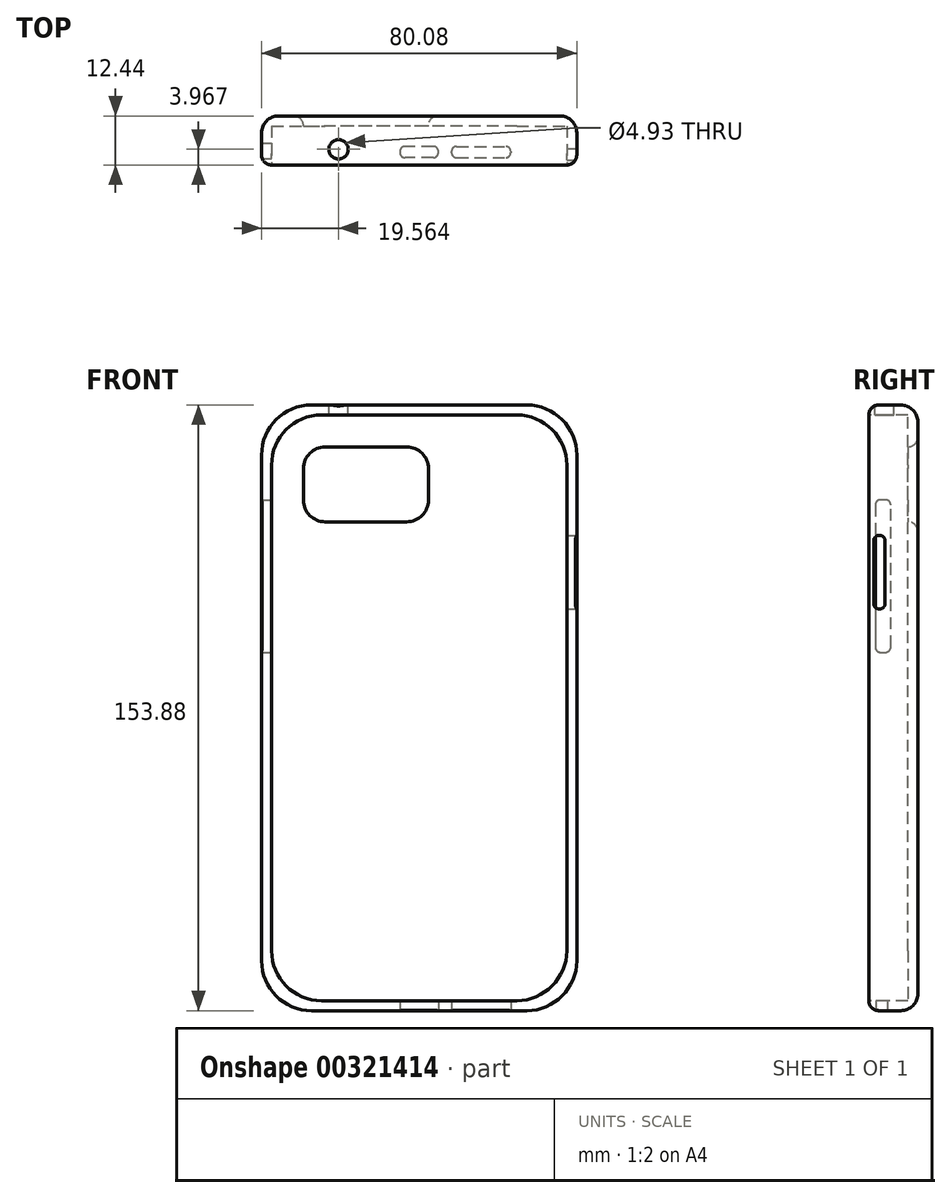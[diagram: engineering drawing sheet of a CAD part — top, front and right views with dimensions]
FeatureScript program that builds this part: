
annotation { "Feature Type Name" : "Feature", "Feature Type Description" : "" }
export const myFeature = defineFeature(function(context is Context, id is Id, definition is map)
    precondition{}
    {
        {
            var Q0;
            Q0=qCreatedBy(makeId("Front.planeOp"),FACE);
            var sketch = newSketch(context, id + "F0", { "sketchPlane" : qUnion([Q0])});
            skLineSegment(sketch, "E0", {"start": v(-36.95, 74.5) * mm, "end": v(38.05, 74.5) * mm});
            skLineSegment(sketch, "E1", {"start": v(38.05, 74.5) * mm, "end": v(38.05, -74.3) * mm});
            skLineSegment(sketch, "E2", {"start": v(38.05, -74.3) * mm, "end": v(-36.95, -74.3) * mm});
            skLineSegment(sketch, "E3", {"start": v(-36.95, -74.3) * mm, "end": v(-36.95, 74.5) * mm});
            skSolve(sketch);
        }
        {
            var Q0;
            Q0=makeQuery(id+"F0.imprint","IMPRINT",FACE,{"disambiguationData":[TD([[makeQuery(id+"F0.imprint","IMPRINT",EDGE,{"derivedFrom":sQuery(id+"F0.wireOp",EDGE,"E0")}),-1.0]])]});
            extrude(context, id + "F1", {"entities" : qUnion([Q0]), "oppositeDirection" : true, "depth" : 9.9 * mm});
        }
        {
            var Q0;
            Q0=makeQuery(id+"F1.opExtrude","SWEPT_FACE",FACE,{"disambiguationData":[OSD([sQuery(id+"F0.wireOp",EDGE,"E3")])]});
            var sketch = newSketch(context, id + "F2", { "sketchPlane" : qUnion([Q0])});
            skLineSegment(sketch, "E4", {"start": v(-5.56, 52.95) * mm, "end": v(-1.65, 52.95) * mm});
            skLineSegment(sketch, "E5", {"start": v(-1.65, 52.95) * mm, "end": v(-1.65, 14.2) * mm});
            skLineSegment(sketch, "E6", {"start": v(-1.65, 14.2) * mm, "end": v(-5.56, 14.2) * mm});
            skLineSegment(sketch, "E7", {"start": v(-5.56, 14.2) * mm, "end": v(-5.56, 52.95) * mm});
            skSolve(sketch);
        }
        {
            var Q0;
            Q0=makeQuery(id+"F1.opExtrude","CAP_FACE",FACE,{"disambiguationData":[OSD([sQuery(id+"F0.wireOp",EDGE,"E0"),sQuery(id+"F0.wireOp",EDGE,"E1"),sQuery(id+"F0.wireOp",EDGE,"E2"),sQuery(id+"F0.wireOp",EDGE,"E3")])],"isStart":true});
            shell(context, id + "F3", {"entities" : qUnion([Q0]), "thickness" : 2.54 * mm, "oppositeDirection" : true});
        }
        {
            var Q0;
            Q0=makeQuery(id+"F2.imprint","IMPRINT",FACE,{"disambiguationData":[TD([[makeQuery(id+"F2.imprint","IMPRINT",EDGE,{"derivedFrom":sQuery(id+"F2.wireOp",EDGE,"E4")}),-1.0]])]});
            extrude(context, id + "F4", {"entities" : qUnion([Q0]), "operationType" : NewBodyOperationType.REMOVE, "oppositeDirection" : true, "depth" : 25.4 * mm});
        }
        {
            var Q0;
            Q0=makeQuery(id+"F1.opExtrude","CAP_EDGE",EDGE,{"disambiguationData":[OSD([sQuery(id+"F0.wireOp",EDGE,"E1")])],"isStart":false});
            var Q1;
            Q1=makeQuery(id+"F1.opExtrude","CAP_EDGE",EDGE,{"disambiguationData":[OSD([sQuery(id+"F0.wireOp",EDGE,"E0")])],"isStart":false});
            var Q2;
            Q2=makeQuery(id+"F1.opExtrude","CAP_EDGE",EDGE,{"disambiguationData":[OSD([sQuery(id+"F0.wireOp",EDGE,"E3")])],"isStart":false});
            var Q3;
            Q3=makeQuery(id+"F1.opExtrude","CAP_EDGE",EDGE,{"disambiguationData":[OSD([sQuery(id+"F0.wireOp",EDGE,"E2")])],"isStart":false});
            fillet(context, id + "F5", {"entities" : qUnion([Q0, Q1, Q2, Q3]), "radius" : 4.3 * mm, "tangentPropagation" : true, "allowEdgeOverflow" : false});
        }
        {
            var Q0;
            Q0=makeQuery(id+"F1.opExtrude","SWEPT_FACE",FACE,{"disambiguationData":[OSD([sQuery(id+"F0.wireOp",EDGE,"E1")])]});
            var sketch = newSketch(context, id + "F6", { "sketchPlane" : qUnion([Q0])});
            skLineSegment(sketch, "E8", {"start": v(1.26, 43.9) * mm, "end": v(4.1, 43.9) * mm});
            skLineSegment(sketch, "E9", {"start": v(4.1, 43.9) * mm, "end": v(4.1, 25.22) * mm});
            skLineSegment(sketch, "E10", {"start": v(4.1, 25.22) * mm, "end": v(1.26, 25.22) * mm});
            skLineSegment(sketch, "E11", {"start": v(1.26, 25.22) * mm, "end": v(1.26, 43.9) * mm});
            skSolve(sketch);
        }
        {
            var Q0;
            Q0=makeQuery(id+"F1.opExtrude","SWEPT_FACE",FACE,{"disambiguationData":[OSD([sQuery(id+"F0.wireOp",EDGE,"E2")])]});
            var sketch = newSketch(context, id + "F7", { "sketchPlane" : qUnion([Q0])});
            skLineSegment(sketch, "E12", {"start": v(-4.33, -1.84) * mm, "end": v(5.42, -1.84) * mm});
            skLineSegment(sketch, "E13", {"start": v(5.42, -1.84) * mm, "end": v(5.42, -4.71) * mm});
            skLineSegment(sketch, "E14", {"start": v(5.42, -4.71) * mm, "end": v(-4.33, -4.71) * mm});
            skLineSegment(sketch, "E15", {"start": v(-4.33, -4.71) * mm, "end": v(-4.33, -1.84) * mm});
            skLineSegment(sketch, "E16", {"start": v(0.55, 0) * mm, "end": v(0.55, -8.15) * mm, "construction": true});
            skPoint(sketch, "E17", {"position": v(0.55, -1.84) * mm});
            skSolve(sketch);
        }
        {
            var Q0;
            Q0=makeQuery(id+"F7.imprint","IMPRINT",FACE,{"disambiguationData":[TD([[makeQuery(id+"F7.imprint","IMPRINT",EDGE,{"derivedFrom":sQuery(id+"F7.wireOp",EDGE,"E12")}),-1.0]])]});
            extrude(context, id + "F8", {"entities" : qUnion([Q0]), "operationType" : NewBodyOperationType.REMOVE, "oppositeDirection" : true, "depth" : 25.4 * mm});
        }
        {
            var Q0;
            Q0=makeQuery(id+"F1.opExtrude","SWEPT_EDGE",EDGE,{"disambiguationData":[OSD([sQuery(id+"F0.wireOp",EDGE,"E0"),sQuery(id+"F0.wireOp",EDGE,"E1")])]});
            var Q1;
            Q1=makeQuery(id+"F1.opExtrude","SWEPT_EDGE",EDGE,{"disambiguationData":[OSD([sQuery(id+"F0.wireOp",EDGE,"E0"),sQuery(id+"F0.wireOp",EDGE,"E3")])]});
            var Q2;
            Q2=makeQuery(id+"F1.opExtrude","SWEPT_EDGE",EDGE,{"disambiguationData":[OSD([sQuery(id+"F0.wireOp",EDGE,"E2"),sQuery(id+"F0.wireOp",EDGE,"E3")])]});
            var Q3;
            Q3=makeQuery(id+"F1.opExtrude","SWEPT_EDGE",EDGE,{"disambiguationData":[OSD([sQuery(id+"F0.wireOp",EDGE,"E1"),sQuery(id+"F0.wireOp",EDGE,"E2")])]});
            var Q4;
            Q4=makeQuery(id+"F3.opShell","OFFSET_EDGE",EDGE,{"disambiguationData":[OSD([sQuery(id+"F0.wireOp",EDGE,"E0"),sQuery(id+"F0.wireOp",EDGE,"E3")])]});
            var Q5;
            Q5=makeQuery(id+"F3.opShell","OFFSET_EDGE",EDGE,{"disambiguationData":[OSD([sQuery(id+"F0.wireOp",EDGE,"E0"),sQuery(id+"F0.wireOp",EDGE,"E1")])]});
            var Q6;
            Q6=makeQuery(id+"F3.opShell","OFFSET_EDGE",EDGE,{"disambiguationData":[OSD([sQuery(id+"F0.wireOp",EDGE,"E1"),sQuery(id+"F0.wireOp",EDGE,"E2")])]});
            var Q7;
            Q7=makeQuery(id+"F3.opShell","OFFSET_EDGE",EDGE,{"disambiguationData":[OSD([sQuery(id+"F0.wireOp",EDGE,"E2"),sQuery(id+"F0.wireOp",EDGE,"E3")])]});
            fillet(context, id + "F9", {"entities" : qUnion([Q0, Q1, Q2, Q3, Q4, Q5, Q6, Q7]), "radius" : 12.7 * mm, "tangentPropagation" : true, "allowEdgeOverflow" : false});
        }
        {
            var Q0;
            Q0=makeQuery(id+"F1.opExtrude","SWEPT_FACE",FACE,{"disambiguationData":[OSD([sQuery(id+"F0.wireOp",EDGE,"E0")])]});
            var sketch = newSketch(context, id + "F10", { "sketchPlane" : qUnion([Q0])});
            skCircle(sketch, "E18", {"center": v(-19.93, 3.97) * mm, "radius": 2.46 * mm});
            skCircle(sketch, "E19", {"center": v(-19.93, 3.97) * mm, "radius": 3.63 * mm});
            skSolve(sketch);
        }
        {
            var Q0;
            {var subQ0=sQuery(id+"F10.wireOp",EDGE,"E18");var subQ1=sQuery(id+"F0.wireOp",EDGE,"E0");var subQ2=makeQuery(id+"F5.opFillet","BLEND_EDGE",EDGE,{"blendedFrom":[makeQuery(id+"F1.opExtrude","CAP_EDGE",EDGE,{"disambiguationData":[OSD([subQ1])],"isStart":false}),makeQuery(id+"F1.opExtrude","SWEPT_FACE",FACE,{"disambiguationData":[OSD([subQ1])]})],"blendedInto":[makeQuery(id+"F1.opExtrude","SWEPT_FACE",FACE,{"disambiguationData":[OSD([subQ1])]})]});var subQ3=makeQuery(id+"F10.imprint","INTERSECT",VERTEX,{"disambiguationData":[OD(0.0)],"derivedFrom":[subQ2,subQ0]});Q0=makeQuery(id+"F10.imprint","IMPRINT",FACE,{"disambiguationData":[TD([[makeQuery(id+"F10.imprint","IMPRINT",EDGE,{"disambiguationData":[TD([[subQ3,-1.0]])],"derivedFrom":subQ0}),1.0]])]});}
            var Q1;
            {var subQ0=sQuery(id+"F10.wireOp",EDGE,"E18");var subQ1=sQuery(id+"F0.wireOp",EDGE,"E0");var subQ2=makeQuery(id+"F5.opFillet","BLEND_EDGE",EDGE,{"blendedFrom":[makeQuery(id+"F1.opExtrude","CAP_EDGE",EDGE,{"disambiguationData":[OSD([subQ1])],"isStart":false}),makeQuery(id+"F1.opExtrude","SWEPT_FACE",FACE,{"disambiguationData":[OSD([subQ1])]})],"blendedInto":[makeQuery(id+"F1.opExtrude","SWEPT_FACE",FACE,{"disambiguationData":[OSD([subQ1])]})]});var subQ3=makeQuery(id+"F10.imprint","INTERSECT",VERTEX,{"disambiguationData":[OD(0.0)],"derivedFrom":[subQ2,subQ0]});Q1=makeQuery(id+"F10.imprint","IMPRINT",FACE,{"disambiguationData":[TD([[makeQuery(id+"F10.imprint","IMPRINT",EDGE,{"disambiguationData":[TD([[subQ3,1.0]])],"derivedFrom":subQ0}),1.0]])]});}
            extrude(context, id + "F11", {"entities" : qUnion([Q0, Q1]), "operationType" : NewBodyOperationType.REMOVE, "oppositeDirection" : true, "depth" : 25.4 * mm});
        }
        {
            var Q0;
            Q0 = qSketchRegion(id + "F6", true);
            extrude(context, id + "F12", {"entities" : qUnion([Q0]), "operationType" : NewBodyOperationType.REMOVE, "oppositeDirection" : true, "depth" : 25.4 * mm});
        }
        {
            var Q0;
            Q0=makeQuery(id+"F1.opExtrude","SWEPT_FACE",FACE,{"disambiguationData":[OSD([sQuery(id+"F0.wireOp",EDGE,"E2")])]});
            var sketch = newSketch(context, id + "F13", { "sketchPlane" : qUnion([Q0])});
            skLineSegment(sketch, "E20", {"start": v(8.8, -1.84) * mm, "end": v(8.8, -4.71) * mm});
            skLineSegment(sketch, "E21", {"start": v(8.8, -4.71) * mm, "end": v(23.82, -4.71) * mm});
            skLineSegment(sketch, "E22", {"start": v(23.82, -4.71) * mm, "end": v(23.82, -1.84) * mm});
            skLineSegment(sketch, "E23", {"start": v(23.82, -1.84) * mm, "end": v(8.8, -1.84) * mm});
            skSolve(sketch);
        }
        {
            var Q0;
            Q0 = qSketchRegion(id + "F13", true);
            extrude(context, id + "F14", {"entities" : qUnion([Q0]), "operationType" : NewBodyOperationType.REMOVE, "oppositeDirection" : true, "depth" : 25.4 * mm});
        }
        {
            var Q0;
            Q0=makeQuery(id+"F1.opExtrude","CAP_EDGE",EDGE,{"disambiguationData":[OSD([sQuery(id+"F0.wireOp",EDGE,"E1")])],"isStart":true});
            var Q1;
            Q1=makeQuery(id+"F1.opExtrude","CAP_EDGE",EDGE,{"disambiguationData":[OSD([sQuery(id+"F0.wireOp",EDGE,"E0")])],"isStart":true});
            var Q2;
            Q2=makeQuery(id+"F1.opExtrude","CAP_EDGE",EDGE,{"disambiguationData":[OSD([sQuery(id+"F0.wireOp",EDGE,"E3")])],"isStart":true});
            var Q3;
            Q3=makeQuery(id+"F1.opExtrude","CAP_EDGE",EDGE,{"disambiguationData":[OSD([sQuery(id+"F0.wireOp",EDGE,"E2")])],"isStart":true});
            fillet(context, id + "F15", {"entities" : qUnion([Q0, Q1, Q2, Q3]), "radius" : 2.54 * mm, "tangentPropagation" : true, "allowEdgeOverflow" : false});
        }
        {
            var Q0;
            Q0=makeQuery(id+"F1.opExtrude","CAP_FACE",FACE,{"disambiguationData":[OSD([sQuery(id+"F0.wireOp",EDGE,"E0"),sQuery(id+"F0.wireOp",EDGE,"E1"),sQuery(id+"F0.wireOp",EDGE,"E2"),sQuery(id+"F0.wireOp",EDGE,"E3")])],"isStart":false});
            var sketch = newSketch(context, id + "F16", { "sketchPlane" : qUnion([Q0])});
            skPoint(sketch, "E24", {"position": v(-0.55, 66.4) * mm});
            skPoint(sketch, "E24.positionSnap0", {"position": v(-0.55, 72.74) * mm});
            skLineSegment(sketch, "E25", {"start": v(-2.9, 66.4) * mm, "end": v(28.85, 66.4) * mm});
            skLineSegment(sketch, "E26", {"start": v(28.85, 66.4) * mm, "end": v(28.85, 47.34) * mm});
            skLineSegment(sketch, "E27", {"start": v(28.85, 47.34) * mm, "end": v(-2.9, 47.34) * mm});
            skLineSegment(sketch, "E28", {"start": v(-2.9, 47.34) * mm, "end": v(-2.9, 66.4) * mm});
            skSolve(sketch);
        }
        {
            var Q0;
            Q0 = qSketchRegion(id + "F16", true);
            extrude(context, id + "F17", {"entities" : qUnion([Q0]), "operationType" : NewBodyOperationType.REMOVE, "oppositeDirection" : true, "depth" : 16.76 * mm});
        }
        {
            var Q0;
            Q0=makeQuery(id+"F17.boolean.opBoolean","COPY",EDGE,{"derivedFrom":makeQuery(id+"F17.opExtrude","SWEPT_EDGE",EDGE,{"disambiguationData":[OSD([sQuery(id+"F16.wireOp",EDGE,"E25"),sQuery(id+"F16.wireOp",EDGE,"E26")])]})});
            var Q1;
            Q1=makeQuery(id+"F17.boolean.opBoolean","COPY",EDGE,{"derivedFrom":makeQuery(id+"F17.opExtrude","SWEPT_EDGE",EDGE,{"disambiguationData":[OSD([sQuery(id+"F16.wireOp",EDGE,"E25"),sQuery(id+"F16.wireOp",EDGE,"E28")])]})});
            var Q2;
            Q2=makeQuery(id+"F17.boolean.opBoolean","COPY",EDGE,{"derivedFrom":makeQuery(id+"F17.opExtrude","SWEPT_EDGE",EDGE,{"disambiguationData":[OSD([sQuery(id+"F16.wireOp",EDGE,"E27"),sQuery(id+"F16.wireOp",EDGE,"E28")])]})});
            var Q3;
            Q3=makeQuery(id+"F17.boolean.opBoolean","COPY",EDGE,{"derivedFrom":makeQuery(id+"F17.opExtrude","SWEPT_EDGE",EDGE,{"disambiguationData":[OSD([sQuery(id+"F16.wireOp",EDGE,"E26"),sQuery(id+"F16.wireOp",EDGE,"E27")])]})});
            fillet(context, id + "F18", {"entities" : qUnion([Q0, Q1, Q2, Q3]), "radius" : 5.52 * mm, "tangentPropagation" : true, "allowEdgeOverflow" : false});
        }
        {
            var Q0;
            Q0=makeQuery(id+"F17.boolean.opBoolean","COPY",EDGE,{"derivedFrom":makeQuery(id+"F17.opExtrude","CAP_EDGE",EDGE,{"disambiguationData":[OSD([sQuery(id+"F16.wireOp",EDGE,"E25")])],"isStart":true})});
            var Q1;
            Q1=makeQuery(id+"F18.opFillet","BLEND_EDGE",EDGE,{"blendedFrom":[makeQuery(id+"F17.boolean.opBoolean","COPY",EDGE,{"derivedFrom":makeQuery(id+"F17.opExtrude","SWEPT_EDGE",EDGE,{"disambiguationData":[OSD([sQuery(id+"F16.wireOp",EDGE,"E25"),sQuery(id+"F16.wireOp",EDGE,"E28")])]})}),makeQuery(id+"F1.opExtrude","CAP_FACE",FACE,{"disambiguationData":[OSD([sQuery(id+"F0.wireOp",EDGE,"E0"),sQuery(id+"F0.wireOp",EDGE,"E1"),sQuery(id+"F0.wireOp",EDGE,"E2"),sQuery(id+"F0.wireOp",EDGE,"E3")])],"isStart":false})],"blendedInto":[makeQuery(id+"F1.opExtrude","CAP_FACE",FACE,{"disambiguationData":[OSD([sQuery(id+"F0.wireOp",EDGE,"E0"),sQuery(id+"F0.wireOp",EDGE,"E1"),sQuery(id+"F0.wireOp",EDGE,"E2"),sQuery(id+"F0.wireOp",EDGE,"E3")])],"isStart":false})]});
            var Q2;
            Q2=makeQuery(id+"F17.boolean.opBoolean","COPY",EDGE,{"derivedFrom":makeQuery(id+"F17.opExtrude","CAP_EDGE",EDGE,{"disambiguationData":[OSD([sQuery(id+"F16.wireOp",EDGE,"E28")])],"isStart":true})});
            var Q3;
            Q3=makeQuery(id+"F18.opFillet","BLEND_EDGE",EDGE,{"blendedFrom":[makeQuery(id+"F17.boolean.opBoolean","COPY",EDGE,{"derivedFrom":makeQuery(id+"F17.opExtrude","SWEPT_EDGE",EDGE,{"disambiguationData":[OSD([sQuery(id+"F16.wireOp",EDGE,"E27"),sQuery(id+"F16.wireOp",EDGE,"E28")])]})}),makeQuery(id+"F1.opExtrude","CAP_FACE",FACE,{"disambiguationData":[OSD([sQuery(id+"F0.wireOp",EDGE,"E0"),sQuery(id+"F0.wireOp",EDGE,"E1"),sQuery(id+"F0.wireOp",EDGE,"E2"),sQuery(id+"F0.wireOp",EDGE,"E3")])],"isStart":false})],"blendedInto":[makeQuery(id+"F1.opExtrude","CAP_FACE",FACE,{"disambiguationData":[OSD([sQuery(id+"F0.wireOp",EDGE,"E0"),sQuery(id+"F0.wireOp",EDGE,"E1"),sQuery(id+"F0.wireOp",EDGE,"E2"),sQuery(id+"F0.wireOp",EDGE,"E3")])],"isStart":false})]});
            var Q4;
            Q4=makeQuery(id+"F17.boolean.opBoolean","COPY",EDGE,{"derivedFrom":makeQuery(id+"F17.opExtrude","CAP_EDGE",EDGE,{"disambiguationData":[OSD([sQuery(id+"F16.wireOp",EDGE,"E27")])],"isStart":true})});
            var Q5;
            Q5=makeQuery(id+"F18.opFillet","BLEND_EDGE",EDGE,{"blendedFrom":[makeQuery(id+"F17.boolean.opBoolean","COPY",EDGE,{"derivedFrom":makeQuery(id+"F17.opExtrude","SWEPT_EDGE",EDGE,{"disambiguationData":[OSD([sQuery(id+"F16.wireOp",EDGE,"E26"),sQuery(id+"F16.wireOp",EDGE,"E27")])]})}),makeQuery(id+"F1.opExtrude","CAP_FACE",FACE,{"disambiguationData":[OSD([sQuery(id+"F0.wireOp",EDGE,"E0"),sQuery(id+"F0.wireOp",EDGE,"E1"),sQuery(id+"F0.wireOp",EDGE,"E2"),sQuery(id+"F0.wireOp",EDGE,"E3")])],"isStart":false})],"blendedInto":[makeQuery(id+"F1.opExtrude","CAP_FACE",FACE,{"disambiguationData":[OSD([sQuery(id+"F0.wireOp",EDGE,"E0"),sQuery(id+"F0.wireOp",EDGE,"E1"),sQuery(id+"F0.wireOp",EDGE,"E2"),sQuery(id+"F0.wireOp",EDGE,"E3")])],"isStart":false})]});
            var Q6;
            Q6=makeQuery(id+"F17.boolean.opBoolean","COPY",EDGE,{"derivedFrom":makeQuery(id+"F17.opExtrude","CAP_EDGE",EDGE,{"disambiguationData":[OSD([sQuery(id+"F16.wireOp",EDGE,"E26")])],"isStart":true})});
            var Q7;
            Q7=makeQuery(id+"F18.opFillet","BLEND_EDGE",EDGE,{"blendedFrom":[makeQuery(id+"F17.boolean.opBoolean","COPY",EDGE,{"derivedFrom":makeQuery(id+"F17.opExtrude","SWEPT_EDGE",EDGE,{"disambiguationData":[OSD([sQuery(id+"F16.wireOp",EDGE,"E25"),sQuery(id+"F16.wireOp",EDGE,"E26")])]})}),makeQuery(id+"F1.opExtrude","CAP_FACE",FACE,{"disambiguationData":[OSD([sQuery(id+"F0.wireOp",EDGE,"E0"),sQuery(id+"F0.wireOp",EDGE,"E1"),sQuery(id+"F0.wireOp",EDGE,"E2"),sQuery(id+"F0.wireOp",EDGE,"E3")])],"isStart":false})],"blendedInto":[makeQuery(id+"F1.opExtrude","CAP_FACE",FACE,{"disambiguationData":[OSD([sQuery(id+"F0.wireOp",EDGE,"E0"),sQuery(id+"F0.wireOp",EDGE,"E1"),sQuery(id+"F0.wireOp",EDGE,"E2"),sQuery(id+"F0.wireOp",EDGE,"E3")])],"isStart":false})]});
            fillet(context, id + "F19", {"entities" : qUnion([Q0, Q1, Q2, Q3, Q4, Q5, Q6, Q7]), "radius" : 2.45 * mm, "tangentPropagation" : true, "allowEdgeOverflow" : false});
        }
        {
            var Q0;
            Q0=makeQuery(id+"F4.boolean.opBoolean","COPY",EDGE,{"derivedFrom":makeQuery(id+"F4.opExtrude","SWEPT_EDGE",EDGE,{"disambiguationData":[OSD([sQuery(id+"F2.wireOp",EDGE,"E6"),sQuery(id+"F2.wireOp",EDGE,"E7")])]})});
            var Q1;
            Q1=makeQuery(id+"F4.boolean.opBoolean","COPY",EDGE,{"derivedFrom":makeQuery(id+"F4.opExtrude","SWEPT_EDGE",EDGE,{"disambiguationData":[OSD([sQuery(id+"F2.wireOp",EDGE,"E5"),sQuery(id+"F2.wireOp",EDGE,"E6")])]})});
            var Q2;
            Q2=makeQuery(id+"F4.boolean.opBoolean","COPY",EDGE,{"derivedFrom":makeQuery(id+"F4.opExtrude","SWEPT_EDGE",EDGE,{"disambiguationData":[OSD([sQuery(id+"F2.wireOp",EDGE,"E4"),sQuery(id+"F2.wireOp",EDGE,"E7")])]})});
            var Q3;
            Q3=makeQuery(id+"F4.boolean.opBoolean","COPY",EDGE,{"derivedFrom":makeQuery(id+"F4.opExtrude","SWEPT_EDGE",EDGE,{"disambiguationData":[OSD([sQuery(id+"F2.wireOp",EDGE,"E4"),sQuery(id+"F2.wireOp",EDGE,"E5")])]})});
            var Q4;
            Q4=makeQuery(id+"F12.boolean.opBoolean","COPY",EDGE,{"derivedFrom":makeQuery(id+"F12.opExtrude","SWEPT_EDGE",EDGE,{"disambiguationData":[OSD([sQuery(id+"F6.wireOp",EDGE,"E9"),sQuery(id+"F6.wireOp",EDGE,"E10")])]})});
            var Q5;
            Q5=makeQuery(id+"F12.boolean.opBoolean","COPY",EDGE,{"derivedFrom":makeQuery(id+"F12.opExtrude","SWEPT_EDGE",EDGE,{"disambiguationData":[OSD([sQuery(id+"F6.wireOp",EDGE,"E8"),sQuery(id+"F6.wireOp",EDGE,"E11")])]})});
            var Q6;
            Q6=makeQuery(id+"F12.boolean.opBoolean","COPY",EDGE,{"derivedFrom":makeQuery(id+"F12.opExtrude","SWEPT_EDGE",EDGE,{"disambiguationData":[OSD([sQuery(id+"F6.wireOp",EDGE,"E10"),sQuery(id+"F6.wireOp",EDGE,"E11")])]})});
            var Q7;
            Q7=makeQuery(id+"F8.boolean.opBoolean","COPY",EDGE,{"derivedFrom":makeQuery(id+"F8.opExtrude","SWEPT_EDGE",EDGE,{"disambiguationData":[OSD([sQuery(id+"F7.wireOp",EDGE,"E14"),sQuery(id+"F7.wireOp",EDGE,"E15")])]})});
            var Q8;
            Q8=makeQuery(id+"F14.boolean.opBoolean","COPY",EDGE,{"derivedFrom":makeQuery(id+"F14.opExtrude","SWEPT_EDGE",EDGE,{"disambiguationData":[OSD([sQuery(id+"F13.wireOp",EDGE,"E20"),sQuery(id+"F13.wireOp",EDGE,"E21")])]})});
            var Q9;
            Q9=makeQuery(id+"F14.boolean.opBoolean","COPY",EDGE,{"derivedFrom":makeQuery(id+"F14.opExtrude","SWEPT_EDGE",EDGE,{"disambiguationData":[OSD([sQuery(id+"F13.wireOp",EDGE,"E21"),sQuery(id+"F13.wireOp",EDGE,"E22")])]})});
            var Q10;
            Q10=makeQuery(id+"F8.boolean.opBoolean","COPY",EDGE,{"derivedFrom":makeQuery(id+"F8.opExtrude","SWEPT_EDGE",EDGE,{"disambiguationData":[OSD([sQuery(id+"F7.wireOp",EDGE,"E13"),sQuery(id+"F7.wireOp",EDGE,"E14")])]})});
            var Q11;
            Q11=makeQuery(id+"F14.boolean.opBoolean","COPY",EDGE,{"derivedFrom":makeQuery(id+"F14.opExtrude","SWEPT_EDGE",EDGE,{"disambiguationData":[OSD([sQuery(id+"F13.wireOp",EDGE,"E22"),sQuery(id+"F13.wireOp",EDGE,"E23")])]})});
            var Q12;
            Q12=makeQuery(id+"F8.boolean.opBoolean","COPY",EDGE,{"derivedFrom":makeQuery(id+"F8.opExtrude","SWEPT_EDGE",EDGE,{"disambiguationData":[OSD([sQuery(id+"F7.wireOp",EDGE,"E12"),sQuery(id+"F7.wireOp",EDGE,"E13")])]})});
            var Q13;
            Q13=makeQuery(id+"F14.boolean.opBoolean","COPY",EDGE,{"derivedFrom":makeQuery(id+"F14.opExtrude","SWEPT_EDGE",EDGE,{"disambiguationData":[OSD([sQuery(id+"F13.wireOp",EDGE,"E20"),sQuery(id+"F13.wireOp",EDGE,"E23")])]})});
            var Q14;
            Q14=makeQuery(id+"F8.boolean.opBoolean","COPY",EDGE,{"derivedFrom":makeQuery(id+"F8.opExtrude","SWEPT_EDGE",EDGE,{"disambiguationData":[OSD([sQuery(id+"F7.wireOp",EDGE,"E12"),sQuery(id+"F7.wireOp",EDGE,"E15")])]})});
            var Q15;
            Q15=makeQuery(id+"F12.boolean.opBoolean","COPY",EDGE,{"derivedFrom":makeQuery(id+"F12.opExtrude","SWEPT_EDGE",EDGE,{"disambiguationData":[OSD([sQuery(id+"F6.wireOp",EDGE,"E8"),sQuery(id+"F6.wireOp",EDGE,"E9")])]})});
            fillet(context, id + "F20", {"entities" : qUnion([Q0, Q1, Q2, Q3, Q4, Q5, Q6, Q7, Q8, Q9, Q10, Q11, Q12, Q13, Q14, Q15]), "radius" : 1.27 * mm, "tangentPropagation" : true, "allowEdgeOverflow" : false});
        }
        {
            var Q0;
            Q0=makeQuery(id+"F2.imprint","IMPRINT",FACE,{"disambiguationData":[TD([[makeQuery(id+"F2.imprint","IMPRINT",EDGE,{"derivedFrom":sQuery(id+"F2.wireOp",EDGE,"E4")}),-1.0]])]});
            extrude(context, id + "F21", {"entities" : qUnion([Q0]), "operationType" : NewBodyOperationType.REMOVE, "depth" : 25.4 * mm});
        }
        {
            var Q0;
            Q0=makeQuery(id+"F21.boolean.opBoolean","COPY",EDGE,{"derivedFrom":makeQuery(id+"F21.opExtrude","SWEPT_EDGE",EDGE,{"disambiguationData":[OSD([sQuery(id+"F2.wireOp",EDGE,"E4"),sQuery(id+"F2.wireOp",EDGE,"E7")])]})});
            var Q1;
            Q1=makeQuery(id+"F21.boolean.opBoolean","COPY",EDGE,{"derivedFrom":makeQuery(id+"F21.opExtrude","SWEPT_EDGE",EDGE,{"disambiguationData":[OSD([sQuery(id+"F2.wireOp",EDGE,"E6"),sQuery(id+"F2.wireOp",EDGE,"E7")])]})});
            var Q2;
            Q2=makeQuery(id+"F21.boolean.opBoolean","COPY",EDGE,{"derivedFrom":makeQuery(id+"F21.opExtrude","SWEPT_EDGE",EDGE,{"disambiguationData":[OSD([sQuery(id+"F2.wireOp",EDGE,"E5"),sQuery(id+"F2.wireOp",EDGE,"E6")])]})});
            var Q3;
            Q3=makeQuery(id+"F21.boolean.opBoolean","COPY",EDGE,{"derivedFrom":makeQuery(id+"F21.opExtrude","SWEPT_EDGE",EDGE,{"disambiguationData":[OSD([sQuery(id+"F2.wireOp",EDGE,"E4"),sQuery(id+"F2.wireOp",EDGE,"E5")])]})});
            fillet(context, id + "F22", {"entities" : qUnion([Q0, Q1, Q2, Q3]), "radius" : 1.27 * mm, "tangentPropagation" : true, "allowEdgeOverflow" : false});
        }
    });
